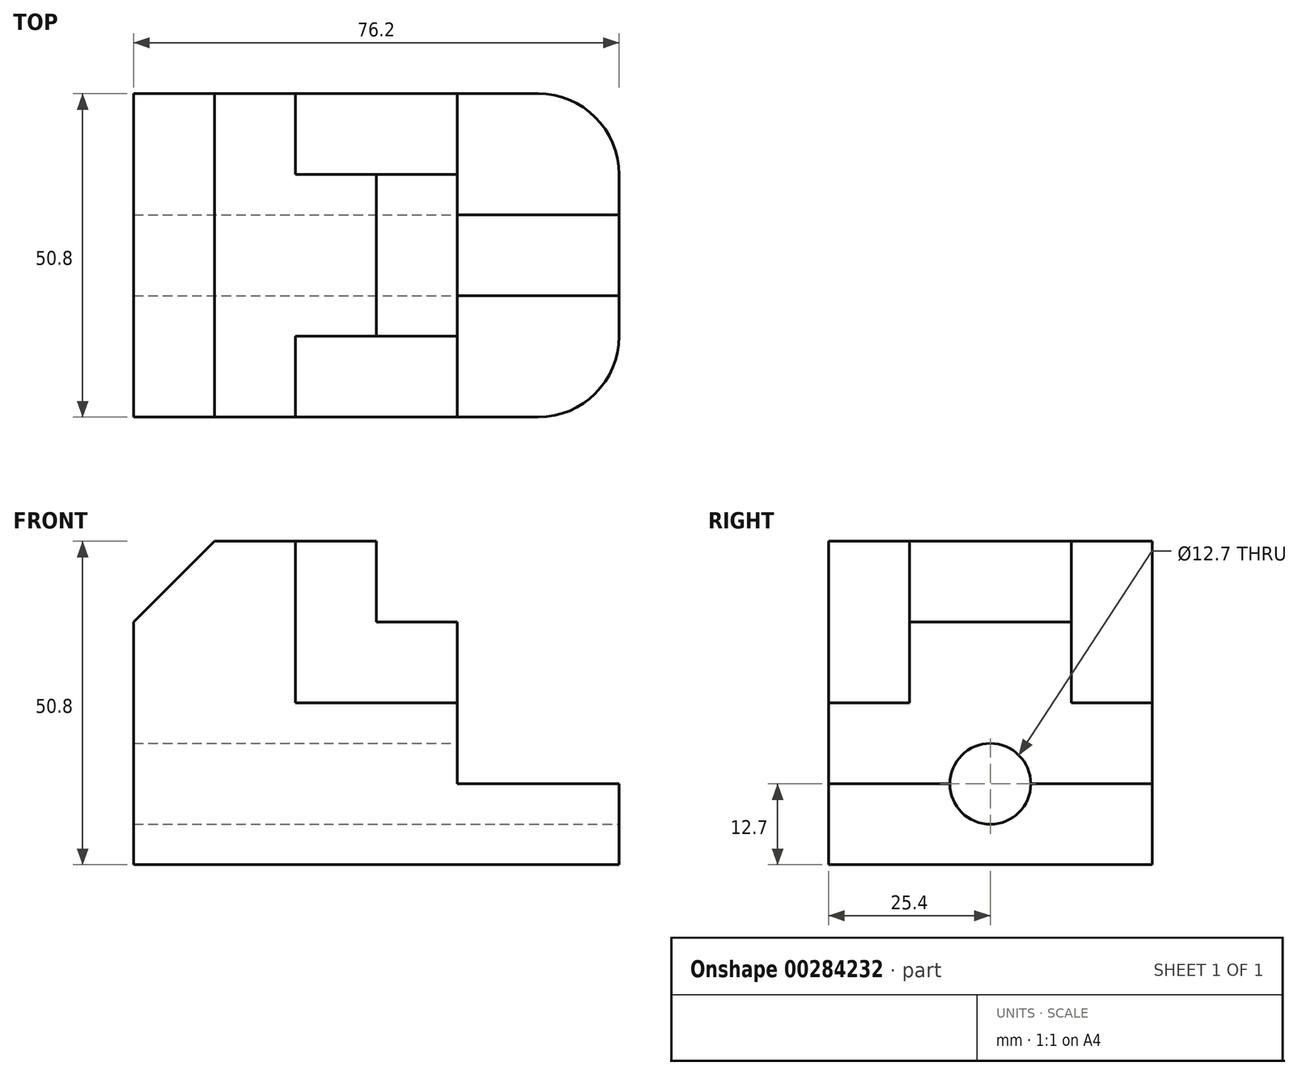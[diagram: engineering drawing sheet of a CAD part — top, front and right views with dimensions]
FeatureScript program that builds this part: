
annotation { "Feature Type Name" : "Feature", "Feature Type Description" : "" }
export const myFeature = defineFeature(function(context is Context, id is Id, definition is map)
    precondition{}
    {
        {
            var Q0;
            Q0=qCreatedBy(makeId("Front.planeOp"),FACE);
            var sketch = newSketch(context, id + "F0", { "sketchPlane" : qUnion([Q0])});
            skLineSegment(sketch, "E0", {"start": v(0, 0) * mm, "end": v(0, 38.1) * mm});
            skLineSegment(sketch, "E1", {"start": v(0, 38.1) * mm, "end": v(12.7, 50.8) * mm});
            skLineSegment(sketch, "E2", {"start": v(12.7, 50.8) * mm, "end": v(38.1, 50.8) * mm});
            skLineSegment(sketch, "E3", {"start": v(38.1, 50.8) * mm, "end": v(38.1, 38.1) * mm});
            skLineSegment(sketch, "E4", {"start": v(38.1, 38.1) * mm, "end": v(50.8, 38.1) * mm});
            skLineSegment(sketch, "E5", {"start": v(50.8, 38.1) * mm, "end": v(50.8, 12.7) * mm});
            skLineSegment(sketch, "E6", {"start": v(50.8, 12.7) * mm, "end": v(76.2, 12.7) * mm});
            skLineSegment(sketch, "E7", {"start": v(76.2, 12.7) * mm, "end": v(76.2, 0) * mm});
            skLineSegment(sketch, "E8", {"start": v(76.2, 0) * mm, "end": v(0, 0) * mm});
            skSolve(sketch);
        }
        {
            var Q0;
            Q0 = qSketchRegion(id + "F0", true);
            extrude(context, id + "F1", {"entities" : qUnion([Q0]), "depth" : 50.8 * mm});
        }
        {
            var Q0;
            Q0=makeQuery(id+"F1.opExtrude","SWEPT_FACE",FACE,{"disambiguationData":[OSD([sQuery(id+"F0.wireOp",EDGE,"E2")])]});
            var sketch = newSketch(context, id + "F2", { "sketchPlane" : qUnion([Q0])});
            skPoint(sketch, "E9.firstSnap0", {"position": v(25.4, -50.8) * mm});
            skLineSegment(sketch, "E9.bottom", {"start": v(50.8, -50.8) * mm, "end": v(25.4, -50.8) * mm});
            skLineSegment(sketch, "E9.top", {"start": v(50.8, -38.1) * mm, "end": v(25.4, -38.1) * mm});
            skLineSegment(sketch, "E9.left", {"start": v(50.8, -50.8) * mm, "end": v(50.8, -38.1) * mm});
            skLineSegment(sketch, "E9.right", {"start": v(25.4, -50.8) * mm, "end": v(25.4, -38.1) * mm});
            skLineSegment(sketch, "E10.bottom", {"start": v(50.8, 0) * mm, "end": v(25.4, 0) * mm});
            skLineSegment(sketch, "E10.top", {"start": v(50.8, -12.7) * mm, "end": v(25.4, -12.7) * mm});
            skLineSegment(sketch, "E10.left", {"start": v(50.8, 0) * mm, "end": v(50.8, -12.7) * mm});
            skLineSegment(sketch, "E10.right", {"start": v(25.4, 0) * mm, "end": v(25.4, -12.7) * mm});
            skSolve(sketch);
        }
        {
            var Q0;
            Q0 = qSketchRegion(id + "F2", true);
            extrude(context, id + "F3", {"entities" : qUnion([Q0]), "operationType" : NewBodyOperationType.REMOVE, "oppositeDirection" : true, "depth" : 25.4 * mm});
        }
        {
            var Q0;
            Q0=makeQuery(id+"F1.opExtrude","SWEPT_FACE",FACE,{"disambiguationData":[OSD([sQuery(id+"F0.wireOp",EDGE,"E7")])]});
            var sketch = newSketch(context, id + "F4", { "sketchPlane" : qUnion([Q0])});
            skCircle(sketch, "E11", {"center": v(-25.4, 12.7) * mm, "radius": 6.35 * mm});
            skSolve(sketch);
        }
        {
            var Q0;
            Q0 = qSketchRegion(id + "F4", true);
            extrude(context, id + "F5", {"entities" : qUnion([Q0]), "operationType" : NewBodyOperationType.REMOVE, "endBound" : BoundingType.THROUGH_ALL, "oppositeDirection" : true, "depth" : 25.4 * mm});
        }
        {
            var Q0;
            Q0=makeQuery(id+"F1.opExtrude","CAP_EDGE",EDGE,{"disambiguationData":[OSD([sQuery(id+"F0.wireOp",EDGE,"E7")])],"isStart":false});
            var Q1;
            Q1=makeQuery(id+"F1.opExtrude","CAP_EDGE",EDGE,{"disambiguationData":[OSD([sQuery(id+"F0.wireOp",EDGE,"E7")])],"isStart":true});
            fillet(context, id + "F6", {"entities" : qUnion([Q0, Q1]), "radius" : 12.7 * mm, "tangentPropagation" : true, "allowEdgeOverflow" : false});
        }
    });
